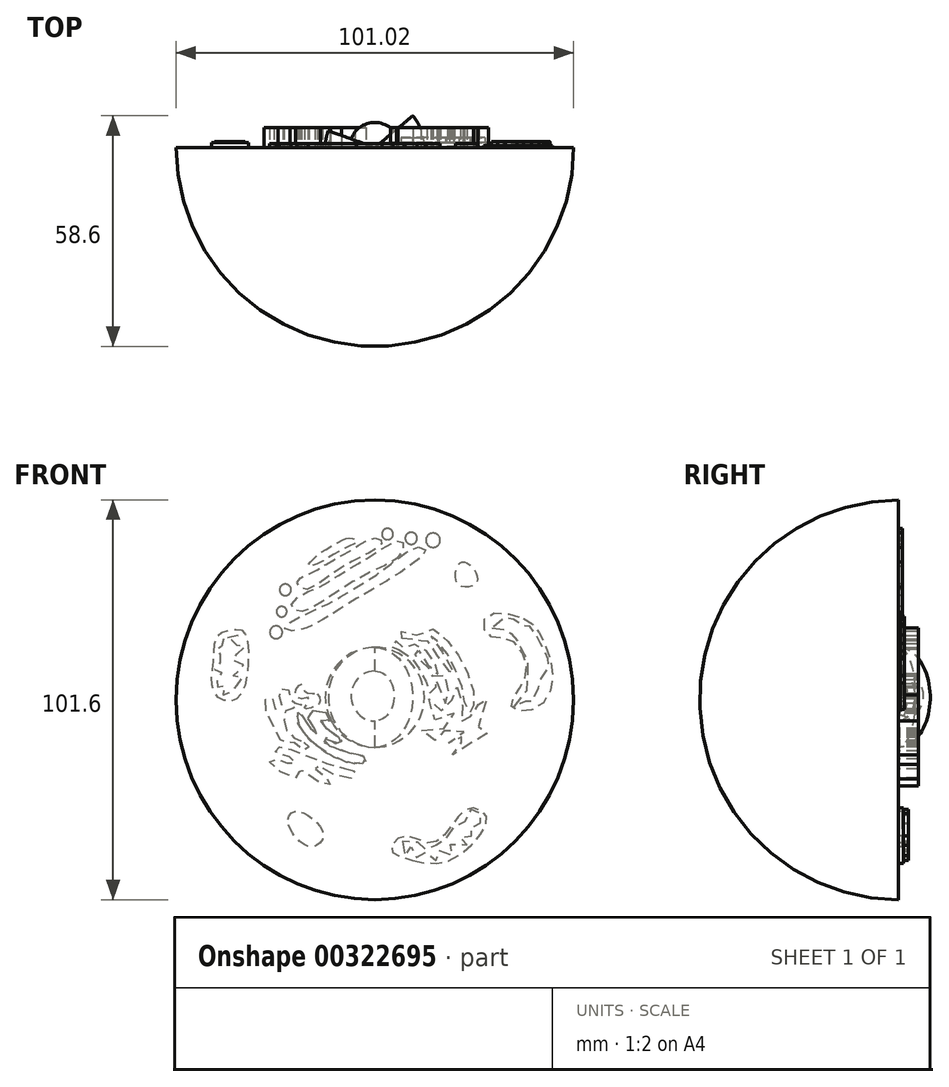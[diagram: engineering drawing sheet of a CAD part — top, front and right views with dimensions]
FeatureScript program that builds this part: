
annotation { "Feature Type Name" : "Feature", "Feature Type Description" : "" }
export const myFeature = defineFeature(function(context is Context, id is Id, definition is map)
    precondition{}
    {
        {
            var Q0;
            Q0=qCreatedBy(makeId("Front.planeOp"),FACE);
            var sketch = newSketch(context, id + "F0", { "sketchPlane" : qUnion([Q0])});
            skLineSegment(sketch, "E0", {"start": v(0, 0) * mm, "end": v(0, 12.7) * mm});
            skArc(sketch, "E1", {"start": v(0, 0) * mm, "mid": v(6.4, 6.35) * mm, "end": v(0, 12.7) * mm});
            skSolve(sketch);
        }
        {
            var Q0;
            Q0=makeQuery(id+"F0.imprint","IMPRINT",FACE,{"disambiguationData":[TD([[makeQuery(id+"F0.imprint","IMPRINT",EDGE,{"derivedFrom":sQuery(id+"F0.wireOp",EDGE,"E0")}),-1.0]])]});
            var Q1;
            Q1=sQuery(id+"F0.wireOp",EDGE,"E0");
            revolve(context, id + "F1", {"entities" : qUnion([Q0]), "axis" : qUnion([Q1]), "revolveType" : RevolveType.FULL});
        }
        {
            var Q0;
            Q0=qCreatedBy(makeId("Front.planeOp"),FACE);
            var sketch = newSketch(context, id + "F2", { "sketchPlane" : qUnion([Q0])});
            skLineSegment(sketch, "E2", {"start": v(0, -6.67) * mm, "end": v(0, 18.73) * mm});
            skArc(sketch, "E3", {"start": v(0, 18.73) * mm, "mid": v(-12.59, 6.03) * mm, "end": v(0, -6.67) * mm});
            skSolve(sketch);
        }
        {
            var Q0;
            Q0=makeQuery(id+"F2.imprint","IMPRINT",FACE,{"disambiguationData":[TD([[makeQuery(id+"F2.imprint","IMPRINT",EDGE,{"derivedFrom":sQuery(id+"F2.wireOp",EDGE,"E2")}),1.0]])]});
            var Q1;
            Q1=sQuery(id+"F2.wireOp",EDGE,"E2");
            revolve(context, id + "F3", {"operationType" : NewBodyOperationType.ADD, "entities" : qUnion([Q0]), "axis" : qUnion([Q1]), "revolveType" : RevolveType.TWO_DIRECTIONS, "angle" : 220 * degree, "angleBack" : 340 * degree});
        }
        {
            var Q0;
            Q0=qCreatedBy(makeId("Right.planeOp"),FACE);
            var sketch = newSketch(context, id + "F4", { "sketchPlane" : qUnion([Q0])});
            skLineSegment(sketch, "E4", {"start": v(0, 56.2) * mm, "end": v(0, -45.4) * mm});
            skArc(sketch, "E5", {"start": v(0, -45.4) * mm, "mid": v(50.5, 5.4) * mm, "end": v(0, 56.2) * mm});
            skSolve(sketch);
        }
        {
            var Q0;
            Q0=makeQuery(id+"F4.imprint","IMPRINT",FACE,{"disambiguationData":[TD([[makeQuery(id+"F4.imprint","IMPRINT",EDGE,{"derivedFrom":sQuery(id+"F4.wireOp",EDGE,"E4")}),1.0]])]});
            var Q1;
            Q1=sQuery(id+"F4.wireOp",EDGE,"E4");
            revolve(context, id + "F5", {"operationType" : NewBodyOperationType.ADD, "entities" : qUnion([Q0]), "axis" : qUnion([Q1]), "revolveType" : RevolveType.TWO_DIRECTIONS, "angle" : 270 * degree, "angleBack" : 90 * degree});
        }
        {
            var Q0;
            Q0=qCreatedBy(makeId("Front.planeOp"),FACE);
            var sketch = newSketch(context, id + "F6", { "sketchPlane" : qUnion([Q0])});
            skFitSpline(sketch, "E6", {"points": [v(9.6, -35.38) * mm, v(18.8, -35.51) * mm, v(27.69, -27.56) * mm, v(27.92, -23.4) * mm, v(23.7, -22.29) * mm, v(19.27, -26.96) * mm, v(14.13, -30.97) * mm, v(7.66, -29.22) * mm, v(4.07, -32.55) * mm, v(9.6, -35.38) * mm]});
            skSolve(sketch);
        }
        {
            var Q0;
            Q0=qSketchRegion(id+"F6",true);
            extrude(context, id + "F7", {"entities" : qUnion([Q0]), "operationType" : NewBodyOperationType.ADD, "oppositeDirection" : true, "depth" : 1.27 * mm});
        }
        {
            var Q0;
            Q0=qCreatedBy(makeId("Front.planeOp"),FACE);
            var sketch = newSketch(context, id + "F8", { "sketchPlane" : qUnion([Q0])});
            skFitSpline(sketch, "E7", {"points": [v(-12.54, 2.24) * mm, v(-11.38, 0) * mm, v(-13.87, 0) * mm, v(-10.61, -3.1) * mm, v(-8.4, -4.96) * mm, v(-9.4, -6.04) * mm, v(-12.52, -4.21) * mm, v(-13.25, -4.93) * mm, v(-5.01, -8.38) * mm, v(-2.42, -9.05) * mm, v(-2.65, -10.58) * mm, v(-11.31, -8.74) * mm, v(-19.67, 0) * mm, v(-19.34, 2.33) * mm, v(-17.66, 0) * mm, v(-14.84, -3.26) * mm, v(-14.58, -2.7) * mm, v(-16.76, 0) * mm, v(-16.36, 2.24) * mm, v(-12.54, 2.24) * mm]});
            skSolve(sketch);
        }
        {
            var Q0;
            Q0=qSketchRegion(id+"F8",true);
            extrude(context, id + "F9", {"entities" : qUnion([Q0]), "operationType" : NewBodyOperationType.ADD, "oppositeDirection" : true, "depth" : 5.08 * mm});
        }
        {
            var Q0;
            Q0=qCreatedBy(makeId("Front.planeOp"),FACE);
            var sketch = newSketch(context, id + "F10", { "sketchPlane" : qUnion([Q0])});
            skFitSpline(sketch, "E8", {"points": [v(-7.66, -12) * mm, v(-5.06, -12.89) * mm, v(-6.93, -14.76) * mm, v(-14.96, -11.24) * mm, v(-14.85, -12.41) * mm, v(-11.5, -15.13) * mm, v(-12, -16.47) * mm, v(-19.37, -12.16) * mm, v(-19.1, -13.6) * mm, v(-20.88, -14.36) * mm, v(-26.72, -10.14) * mm, v(-23.75, -9.96) * mm, v(-21.5, -10.92) * mm, v(-19.93, -10.03) * mm, v(-25.5, -7.67) * mm, v(-24.28, -6.65) * mm, v(-19.24, -8.06) * mm, v(-7.66, -12) * mm]});
            skSolve(sketch);
        }
        {
            var Q0;
            Q0=qSketchRegion(id+"F10",true);
            extrude(context, id + "F11", {"entities" : qUnion([Q0]), "operationType" : NewBodyOperationType.ADD, "oppositeDirection" : true, "depth" : 5.08 * mm});
        }
        {
            var Q0;
            Q0=qCreatedBy(makeId("Front.planeOp"),FACE);
            var sketch = newSketch(context, id + "F12", { "sketchPlane" : qUnion([Q0])});
            skFitSpline(sketch, "E9", {"points": [v(-17.95, -5.44) * mm, v(-16.66, -6.4) * mm, v(-17.8, -7.6) * mm, v(-21.09, -5.17) * mm, v(-23, -5.57) * mm, v(-25.04, -2.63) * mm, v(-28.02, 4.97) * mm, v(-26.26, 5.94) * mm, v(-25.15, 2.95) * mm, v(-23.37, 4.5) * mm, v(-24.55, 7.26) * mm, v(-22.55, 8.42) * mm, v(-21.57, 6.57) * mm, v(-21.12, 4.79) * mm, v(-18.57, 4.3) * mm, v(-20.32, 3.37) * mm, v(-22.58, 2.7) * mm, v(-22.98, 0) * mm, v(-21.6, -3.48) * mm, v(-17.95, -5.44) * mm]});
            skSolve(sketch);
        }
        {
            var Q0;
            Q0=qSketchRegion(id+"F12",true);
            extrude(context, id + "F13", {"entities" : qUnion([Q0]), "operationType" : NewBodyOperationType.ADD, "oppositeDirection" : true, "depth" : 5.08 * mm});
        }
        {
            var Q0;
            Q0=qCreatedBy(makeId("Front.planeOp"),FACE);
            var sketch = newSketch(context, id + "F14", { "sketchPlane" : qUnion([Q0])});
            skFitSpline(sketch, "E10", {"points": [v(-14.63, 6.86) * mm, v(-13.89, 4.93) * mm, v(-15.24, 3.7) * mm, v(-17.79, 3.21) * mm, v(-17, 4.7) * mm, v(-17.02, 5.09) * mm, v(-16.9, 5.99) * mm, v(-18.89, 5.63) * mm, v(-20.14, 7.6) * mm, v(-18.37, 9.4) * mm, v(-17.73, 7.4) * mm, v(-14.63, 6.86) * mm]});
            skSolve(sketch);
        }
        {
            var Q0;
            Q0=qSketchRegion(id+"F14",true);
            extrude(context, id + "F15", {"entities" : qUnion([Q0]), "operationType" : NewBodyOperationType.ADD, "oppositeDirection" : true, "depth" : 5.08 * mm});
        }
        {
            var Q0;
            Q0=qCreatedBy(makeId("Front.planeOp"),FACE);
            var sketch = newSketch(context, id + "F16", { "sketchPlane" : qUnion([Q0])});
            skFitSpline(sketch, "E11", {"points": [v(6.06, 18.18) * mm, v(9.04, 16.45) * mm, v(10.42, 14.53) * mm, v(12.01, 12.23) * mm, v(13.1, 9.44) * mm, v(13.54, 7.45) * mm, v(15.68, 7.3) * mm, v(15.32, 9.12) * mm, v(14.84, 10.01) * mm, v(15.82, 10.44) * mm, v(16.73, 8.54) * mm, v(17.09, 5.02) * mm, v(18.51, 4.63) * mm, v(18.74, 7.34) * mm, v(17.99, 11.49) * mm, v(15.64, 11.5) * mm, v(14.6, 11.35) * mm, v(14.4, 12.08) * mm, v(12.35, 14.95) * mm, v(9.73, 17.64) * mm, v(10.7, 18.17) * mm, v(12.55, 15.85) * mm, v(14.8, 12.58) * mm, v(16.28, 12.09) * mm, v(16.18, 13.1) * mm, v(14.22, 15.94) * mm, v(12.17, 18.88) * mm, v(9.92, 19.42) * mm, v(8.6, 18.46) * mm, v(5.63, 19.43) * mm, v(5.5, 20.24) * mm, v(4.46, 20.6) * mm, v(4.1, 18.83) * mm, v(5.01, 18.62) * mm, v(6.06, 18.18) * mm]});
            skSolve(sketch);
        }
        {
            var Q0;
            Q0=qSketchRegion(id+"F16",true);
            extrude(context, id + "F17", {"entities" : qUnion([Q0]), "operationType" : NewBodyOperationType.ADD, "oppositeDirection" : true, "depth" : 5.08 * mm});
        }
        {
            var Q0;
            Q0=makeQuery(id+"F5.opRevolve","CAP_FACE",FACE,{"disambiguationData":[OSD([sQuery(id+"F4.wireOp",EDGE,"E4"),sQuery(id+"F4.wireOp",EDGE,"E5")])],"isStart":false});
            var sketch = newSketch(context, id + "F18", { "sketchPlane" : qUnion([Q0])});
            skFitSpline(sketch, "E12", {"points": [v(-6.93, 21.04) * mm, v(-6.03, 22.56) * mm, v(-9.3, 22.38) * mm, v(-11.99, 21.66) * mm, v(-12.96, 22.73) * mm, v(-14.23, 23.62) * mm, v(-18.95, 19.87) * mm, v(-21.84, 15.47) * mm, v(-24.8, 8.95) * mm, v(-25.12, 4.58) * mm, v(-24.88, 2.71) * mm, v(-24.08, 2.18) * mm, v(-22.87, 4.23) * mm, v(-22.16, 8.57) * mm, v(-20.3, 13.3) * mm, v(-17.4, 18.62) * mm, v(-14.81, 21.23) * mm, v(-14.26, 21.66) * mm, v(-17.85, 16.4) * mm, v(-20.2, 11.52) * mm, v(-17.49, 14.4) * mm, v(-13.96, 19.62) * mm, v(-13.06, 20.69) * mm, v(-12.6, 20.53) * mm, v(-6.93, 21.04) * mm]});
            skSolve(sketch);
        }
        {
            var Q0;
            Q0=qSketchRegion(id+"F18",true);
            extrude(context, id + "F19", {"entities" : qUnion([Q0]), "operationType" : NewBodyOperationType.ADD, "depth" : 5.08 * mm});
        }
        {
            var Q0;
            Q0=qCreatedBy(makeId("Front.planeOp"),FACE);
            var sketch = newSketch(context, id + "F20", { "sketchPlane" : qUnion([Q0])});
            skFitSpline(sketch, "E13", {"points": [v(20.84, 8.67) * mm, v(21.74, 6.16) * mm, v(22.38, 2.3) * mm, v(21.8, 0) * mm, v(22.9, 0) * mm, v(24.08, 0) * mm, v(24.52, 1.6) * mm, v(26.44, 2.81) * mm, v(26.19, 5.44) * mm, v(27.83, 6.55) * mm, v(28.46, 1.7) * mm, v(26.04, 0) * mm, v(25.74, -2.1) * mm, v(27.64, 0) * mm, v(28.43, -3.18) * mm, v(18.84, -8.59) * mm, v(21.9, -5.56) * mm, v(23.4, -4.19) * mm, v(22.73, -3.8) * mm, v(20.61, -5.18) * mm, v(19.24, -5.88) * mm, v(18.56, -4.71) * mm, v(22.72, -2.6) * mm, v(21.37, -1.88) * mm, v(15.94, -3.55) * mm, v(15.98, -4.69) * mm, v(13.97, -4.47) * mm, v(11.7, -2.4) * mm, v(15.05, -2.82) * mm, v(19.34, 0) * mm, v(20.2, 2) * mm, v(17.73, 0) * mm, v(13.69, 2.03) * mm, v(13.86, 5.65) * mm, v(15.47, 3.92) * mm, v(17.62, 2.44) * mm, v(19.7, 4.12) * mm, v(19.3, 8.32) * mm, v(20.84, 8.67) * mm]});
            skSolve(sketch);
        }
        {
            var Q0;
            Q0=qSketchRegion(id+"F20",true);
            extrude(context, id + "F21", {"entities" : qUnion([Q0]), "operationType" : NewBodyOperationType.ADD, "oppositeDirection" : true, "depth" : 5.08 * mm});
        }
        {
            var Q0;
            Q0=qCreatedBy(makeId("Front.planeOp"),FACE);
            var sketch = newSketch(context, id + "F22", { "sketchPlane" : qUnion([Q0])});
            skFitSpline(sketch, "E14", {"points": [v(7.07, -30.62) * mm, v(6.9, -33.28) * mm, v(7.92, -34.2) * mm, v(8.44, -31.66) * mm, v(9.73, -32.89) * mm, v(9.74, -34.33) * mm, v(11.72, -34.5) * mm, v(12.04, -33.65) * mm, v(13.6, -33.47) * mm, v(14.29, -35) * mm, v(16.22, -35.2) * mm, v(15.97, -33.26) * mm, v(16.8, -32.85) * mm, v(18.72, -34.08) * mm, v(20.02, -33.63) * mm, v(18.97, -31.8) * mm, v(20.06, -31.08) * mm, v(22.97, -31.55) * mm, v(24.4, -30.22) * mm, v(21.38, -29.57) * mm, v(22.54, -29.08) * mm, v(25.5, -28.92) * mm, v(25.4, -27.59) * mm, v(24.24, -26.97) * mm, v(25.6, -25.93) * mm, v(27.53, -25.53) * mm, v(27.66, -23.5) * mm, v(25.06, -23.91) * mm, v(24.67, -22.5) * mm, v(22.51, -23.7) * mm, v(22.73, -25.94) * mm, v(20.31, -26.2) * mm, v(20.06, -28.48) * mm, v(19.4, -29.36) * mm, v(17.97, -29.29) * mm, v(18.21, -30.66) * mm, v(16.77, -30.55) * mm, v(16.38, -31.64) * mm, v(16.1, -31.85) * mm, v(14.58, -31.22) * mm, v(13.46, -32.32) * mm, v(12.07, -32.25) * mm, v(11.32, -30.59) * mm, v(9.9, -31.48) * mm, v(7.07, -30.62) * mm]});
            skSolve(sketch);
        }
        {
            var Q0;
            Q0=qSketchRegion(id+"F22",true);
            extrude(context, id + "F23", {"entities" : qUnion([Q0]), "operationType" : NewBodyOperationType.ADD, "oppositeDirection" : true, "depth" : 2.54 * mm});
        }
        {
            var Q0;
            Q0=qCreatedBy(makeId("Front.planeOp"),FACE);
            var sketch = newSketch(context, id + "F24", { "sketchPlane" : qUnion([Q0])});
            skFitSpline(sketch, "E15", {"points": [v(-35.22, 23.3) * mm, v(-32.99, 22.24) * mm, v(-32.42, 11.9) * mm, v(-35.24, 5.52) * mm, v(-39.19, 5.61) * mm, v(-41.42, 9.47) * mm, v(-40.9, 15.68) * mm, v(-39.94, 21.72) * mm, v(-35.22, 23.3) * mm]});
            skSolve(sketch);
        }
        {
            var Q0;
            Q0=qSketchRegion(id+"F24",true);
            extrude(context, id + "F25", {"entities" : qUnion([Q0]), "operationType" : NewBodyOperationType.ADD, "oppositeDirection" : true, "depth" : 1.27 * mm});
        }
        {
            var Q0;
            Q0=qCreatedBy(makeId("Front.planeOp"),FACE);
            var sketch = newSketch(context, id + "F26", { "sketchPlane" : qUnion([Q0])});
            skFitSpline(sketch, "E16", {"points": [v(-38.38, 20.87) * mm, v(-38.67, 18.96) * mm, v(-39.24, 18.98) * mm, v(-40.09, 18.38) * mm, v(-40.23, 17.4) * mm, v(-39.28, 16.97) * mm, v(-38.95, 15.21) * mm, v(-40.42, 14.18) * mm, v(-40.48, 12.66) * mm, v(-38.92, 12.44) * mm, v(-39.42, 11.1) * mm, v(-40.5, 10.1) * mm, v(-39.69, 8.63) * mm, v(-38.08, 9.1) * mm, v(-39.21, 7.42) * mm, v(-36.8, 6.47) * mm, v(-36.14, 8.7) * mm, v(-34.2, 9.35) * mm, v(-33.67, 11.04) * mm, v(-35.92, 11.36) * mm, v(-35.83, 12.33) * mm, v(-33.86, 12.88) * mm, v(-33.4, 14.34) * mm, v(-35.85, 15.27) * mm, v(-35.78, 16.74) * mm, v(-33.64, 17.72) * mm, v(-33.16, 19.57) * mm, v(-35.9, 19.2) * mm, v(-36.38, 20.65) * mm, v(-34.52, 21.67) * mm, v(-38.38, 20.87) * mm]});
            skSolve(sketch);
        }
        {
            var Q0;
            Q0=qSketchRegion(id+"F26",true);
            extrude(context, id + "F27", {"entities" : qUnion([Q0]), "operationType" : NewBodyOperationType.ADD, "oppositeDirection" : true, "depth" : 1.5 * mm});
        }
        {
            var Q0;
            Q0=qCreatedBy(makeId("Front.planeOp"),FACE);
            var sketch = newSketch(context, id + "F28", { "sketchPlane" : qUnion([Q0])});
            skFitSpline(sketch, "E17", {"points": [v(37.75, 26.12) * mm, v(41.7, 22.44) * mm, v(45.2, 11.92) * mm, v(41.06, 3.27) * mm, v(34.92, 3.37) * mm, v(36.04, 7.2) * mm, v(38.63, 13.08) * mm, v(34.49, 20.58) * mm, v(28.75, 21.9) * mm, v(28.44, 26.66) * mm, v(37.75, 26.12) * mm]});
            skSolve(sketch);
        }
        {
            var Q0;
            Q0=qSketchRegion(id+"F28",true);
            extrude(context, id + "F29", {"entities" : qUnion([Q0]), "operationType" : NewBodyOperationType.ADD, "oppositeDirection" : true, "depth" : 0.5 * mm});
        }
        {
            var Q0;
            Q0=qCreatedBy(makeId("Front.planeOp"),FACE);
            var sketch = newSketch(context, id + "F30", { "sketchPlane" : qUnion([Q0])});
            skFitSpline(sketch, "E18", {"points": [v(29.83, 23.6) * mm, v(30.19, 22.21) * mm, v(31.39, 22.03) * mm, v(32.26, 23.2) * mm, v(33.22, 23.04) * mm, v(32.58, 21.85) * mm, v(34.08, 21.4) * mm, v(34.63, 22.2) * mm, v(34.85, 22.63) * mm, v(35.43, 22.32) * mm, v(34.8, 21.05) * mm, v(36.21, 20.18) * mm, v(37.15, 21.3) * mm, v(37.6, 20.53) * mm, v(36.57, 19.54) * mm, v(37.25, 18.68) * mm, v(38.4, 19.02) * mm, v(38.9, 18.21) * mm, v(37.93, 17.62) * mm, v(38.37, 16.47) * mm, v(39.46, 16.76) * mm, v(39.75, 15.7) * mm, v(38.92, 15.13) * mm, v(39.08, 14.3) * mm, v(40.06, 13.87) * mm, v(39.85, 11.68) * mm, v(38.67, 11.52) * mm, v(39.05, 10.11) * mm, v(37.96, 8.9) * mm, v(38.6, 7.86) * mm, v(36.96, 6.94) * mm, v(35.52, 5.03) * mm, v(35.22, 3.78) * mm, v(36.92, 4.1) * mm, v(37.15, 5.33) * mm, v(38.18, 5.78) * mm, v(38.38, 4.54) * mm, v(38.07, 3.24) * mm, v(39.49, 3.18) * mm, v(40.06, 5.76) * mm, v(40.62, 7.11) * mm, v(42.37, 7.42) * mm, v(41.36, 8.74) * mm, v(41.48, 9.64) * mm, v(43.9, 9.75) * mm, v(41.84, 10.96) * mm, v(42.13, 11.7) * mm, v(44.15, 11.8) * mm, v(44.24, 13.71) * mm, v(42.74, 14.09) * mm, v(42.79, 14.46) * mm, v(44.01, 14.72) * mm, v(43.95, 15.78) * mm, v(42.66, 15.81) * mm, v(42.63, 16.3) * mm, v(43.36, 16.33) * mm, v(43.22, 17.8) * mm, v(42.25, 17.29) * mm, v(42.1, 17.97) * mm, v(42.8, 18.49) * mm, v(42.13, 19.74) * mm, v(41.25, 19.3) * mm, v(40.75, 19.89) * mm, v(41.66, 20.88) * mm, v(40.95, 21.92) * mm, v(39.68, 21.57) * mm, v(39.38, 21.84) * mm, v(39.86, 23.12) * mm, v(39.3, 24.07) * mm, v(38.02, 22.77) * mm, v(37.48, 22.87) * mm, v(37.74, 24.61) * mm, v(36.4, 23.03) * mm, v(35.73, 23.38) * mm, v(36.15, 25.1) * mm, v(34.5, 25.77) * mm, v(33.36, 24.07) * mm, v(32.87, 24.15) * mm, v(32.9, 26.22) * mm, v(31.21, 26.14) * mm, v(31.35, 24.36) * mm, v(29.83, 23.6) * mm]});
            skSolve(sketch);
        }
        {
            var Q0;
            Q0=qSketchRegion(id+"F30",true);
            extrude(context, id + "F31", {"entities" : qUnion([Q0]), "operationType" : NewBodyOperationType.ADD, "oppositeDirection" : true, "depth" : 1.5 * mm});
        }
        {
            var Q0;
            Q0=qCreatedBy(makeId("Front.planeOp"),FACE);
            var sketch = newSketch(context, id + "F32", { "sketchPlane" : qUnion([Q0])});
            skFitSpline(sketch, "E19", {"points": [v(-8.18, 45.99) * mm, v(-6.17, 46.5) * mm, v(-4.6, 45.63) * mm, v(-7.3, 44.05) * mm, v(-13.05, 40.8) * mm, v(-16.9, 39.29) * mm, v(-15.03, 41.73) * mm, v(-8.18, 45.99) * mm]});
            skSolve(sketch);
        }
        {
            var Q0;
            Q0=qSketchRegion(id+"F32",true);
            extrude(context, id + "F33", {"entities" : qUnion([Q0]), "operationType" : NewBodyOperationType.ADD, "oppositeDirection" : true, "depth" : 1 * mm});
        }
        {
            var Q0;
            Q0=qCreatedBy(makeId("Front.planeOp"),FACE);
            var sketch = newSketch(context, id + "F34", { "sketchPlane" : qUnion([Q0])});
            skFitSpline(sketch, "E20", {"points": [v(0, 46.47) * mm, v(1.88, 45.56) * mm, v(0, 43.6) * mm, v(-5.33, 40.8) * mm, v(-10.7, 37.52) * mm, v(-18.13, 33.43) * mm, v(-19.77, 35.4) * mm, v(-16.67, 37.39) * mm, v(-10.36, 41.02) * mm, v(-5.44, 43.76) * mm, v(0, 46.47) * mm]});
            skSolve(sketch);
        }
        {
            var Q0;
            Q0=qSketchRegion(id+"F34",true);
            extrude(context, id + "F35", {"entities" : qUnion([Q0]), "operationType" : NewBodyOperationType.ADD, "oppositeDirection" : true, "depth" : 1 * mm});
        }
        {
            var Q0;
            Q0=qCreatedBy(makeId("Front.planeOp"),FACE);
            var sketch = newSketch(context, id + "F36", { "sketchPlane" : qUnion([Q0])});
            skFitSpline(sketch, "E21", {"points": [v(5.62, 45.69) * mm, v(7.2, 45.3) * mm, v(6.6, 42.24) * mm, v(-1.88, 37.45) * mm, v(-14.25, 29.75) * mm, v(-18.88, 27.86) * mm, v(-21.17, 28.8) * mm, v(-19.5, 31.54) * mm, v(-14.37, 33.94) * mm, v(-9.1, 37.08) * mm, v(-3.9, 40.2) * mm, v(0, 42.63) * mm, v(5.62, 45.69) * mm]});
            skSolve(sketch);
        }
        {
            var Q0;
            Q0=qSketchRegion(id+"F36",true);
            extrude(context, id + "F37", {"entities" : qUnion([Q0]), "operationType" : NewBodyOperationType.ADD, "oppositeDirection" : true, "depth" : 1 * mm});
        }
        {
            var Q0;
            Q0=qCreatedBy(makeId("Front.planeOp"),FACE);
            var sketch = newSketch(context, id + "F38", { "sketchPlane" : qUnion([Q0])});
            skFitSpline(sketch, "E22", {"points": [v(11.13, 44.25) * mm, v(12.91, 43.24) * mm, v(10.64, 40.7) * mm, v(3.6, 35.95) * mm, v(-7.41, 29.39) * mm, v(-19.44, 23) * mm, v(-22.92, 23.5) * mm, v(-19.3, 26.3) * mm, v(-12.19, 29.64) * mm, v(-5.7, 33.39) * mm, v(1.65, 38.03) * mm, v(11.13, 44.25) * mm]});
            skSolve(sketch);
        }
        {
            var Q0;
            Q0=qSketchRegion(id+"F38",true);
            extrude(context, id + "F39", {"entities" : qUnion([Q0]), "operationType" : NewBodyOperationType.ADD, "oppositeDirection" : true, "depth" : 1 * mm});
        }
        {
            var Q0;
            Q0=qCreatedBy(makeId("Front.planeOp"),FACE);
            var sketch = newSketch(context, id + "F40", { "sketchPlane" : qUnion([Q0])});
            skCircle(sketch, "E23", {"center": v(-22.73, 33.32) * mm, "radius": 1.46 * mm});
            skSolve(sketch);
        }
        {
            var Q0;
            Q0=qSketchRegion(id+"F40",true);
            extrude(context, id + "F41", {"entities" : qUnion([Q0]), "operationType" : NewBodyOperationType.ADD, "oppositeDirection" : true, "depth" : 1 * mm});
        }
        {
            var Q0;
            Q0=qCreatedBy(makeId("Front.planeOp"),FACE);
            var sketch = newSketch(context, id + "F42", { "sketchPlane" : qUnion([Q0])});
            skCircle(sketch, "E24", {"center": v(-23.65, 27.79) * mm, "radius": 1.32 * mm});
            skSolve(sketch);
        }
        {
            var Q0;
            Q0=qSketchRegion(id+"F42",true);
            extrude(context, id + "F43", {"entities" : qUnion([Q0]), "operationType" : NewBodyOperationType.ADD, "oppositeDirection" : true, "depth" : 1 * mm});
        }
        {
            var Q0;
            Q0=qCreatedBy(makeId("Front.planeOp"),FACE);
            var sketch = newSketch(context, id + "F44", { "sketchPlane" : qUnion([Q0])});
            skCircle(sketch, "E25", {"center": v(3.24, 47.5) * mm, "radius": 1.44 * mm});
            skSolve(sketch);
        }
        {
            var Q0;
            Q0=qSketchRegion(id+"F44",true);
            extrude(context, id + "F45", {"entities" : qUnion([Q0]), "operationType" : NewBodyOperationType.ADD, "oppositeDirection" : true, "depth" : 1 * mm});
        }
        {
            var Q0;
            Q0=qCreatedBy(makeId("Front.planeOp"),FACE);
            var sketch = newSketch(context, id + "F46", { "sketchPlane" : qUnion([Q0])});
            skCircle(sketch, "E26", {"center": v(9.24, 46.43) * mm, "radius": 1.53 * mm});
            skSolve(sketch);
        }
        {
            var Q0;
            Q0=qSketchRegion(id+"F46",true);
            extrude(context, id + "F47", {"entities" : qUnion([Q0]), "operationType" : NewBodyOperationType.ADD, "oppositeDirection" : true, "depth" : 1 * mm});
        }
        {
            var Q0;
            Q0=qCreatedBy(makeId("Front.planeOp"),FACE);
            var sketch = newSketch(context, id + "F48", { "sketchPlane" : qUnion([Q0])});
            skCircle(sketch, "E27", {"center": v(-25.08, 22.56) * mm, "radius": 1.6 * mm});
            skSolve(sketch);
        }
        {
            var Q0;
            Q0=qSketchRegion(id+"F48",true);
            extrude(context, id + "F49", {"entities" : qUnion([Q0]), "operationType" : NewBodyOperationType.ADD, "oppositeDirection" : true, "depth" : 1 * mm});
        }
        {
            var Q0;
            Q0=qCreatedBy(makeId("Front.planeOp"),FACE);
            var sketch = newSketch(context, id + "F50", { "sketchPlane" : qUnion([Q0])});
            skCircle(sketch, "E28", {"center": v(14.8, 45.94) * mm, "radius": 1.81 * mm});
            skSolve(sketch);
        }
        {
            var Q0;
            Q0=qSketchRegion(id+"F50",true);
            extrude(context, id + "F51", {"entities" : qUnion([Q0]), "operationType" : NewBodyOperationType.ADD, "oppositeDirection" : true, "depth" : 1 * mm});
        }
        {
            var Q0;
            Q0=qCreatedBy(makeId("Front.planeOp"),FACE);
            var sketch = newSketch(context, id + "F52", { "sketchPlane" : qUnion([Q0])});
            skFitSpline(sketch, "E29", {"points": [v(21.61, 40.1) * mm, v(23.48, 40.1) * mm, v(25.85, 37.42) * mm, v(25.49, 34.76) * mm, v(22.1, 34.25) * mm, v(20.5, 36.24) * mm, v(21.61, 40.1) * mm]});
            skSolve(sketch);
        }
        {
            var Q0;
            Q0=qSketchRegion(id+"F52",true);
            extrude(context, id + "F53", {"entities" : qUnion([Q0]), "operationType" : NewBodyOperationType.ADD, "oppositeDirection" : true, "depth" : 1 * mm});
        }
        {
            var Q0;
            Q0=qCreatedBy(makeId("Front.planeOp"),FACE);
            var sketch = newSketch(context, id + "F54", { "sketchPlane" : qUnion([Q0])});
            skFitSpline(sketch, "E30", {"points": [v(-22.02, -25.03) * mm, v(-20.3, -23) * mm, v(-15.65, -24.92) * mm, v(-13.11, -29.2) * mm, v(-15.6, -31.93) * mm, v(-19.86, -29.8) * mm, v(-22.02, -25.03) * mm]});
            skSolve(sketch);
        }
        {
            var Q0;
            Q0=qSketchRegion(id+"F54",true);
            extrude(context, id + "F55", {"entities" : qUnion([Q0]), "operationType" : NewBodyOperationType.ADD, "oppositeDirection" : true, "depth" : 1 * mm});
        }
    });
